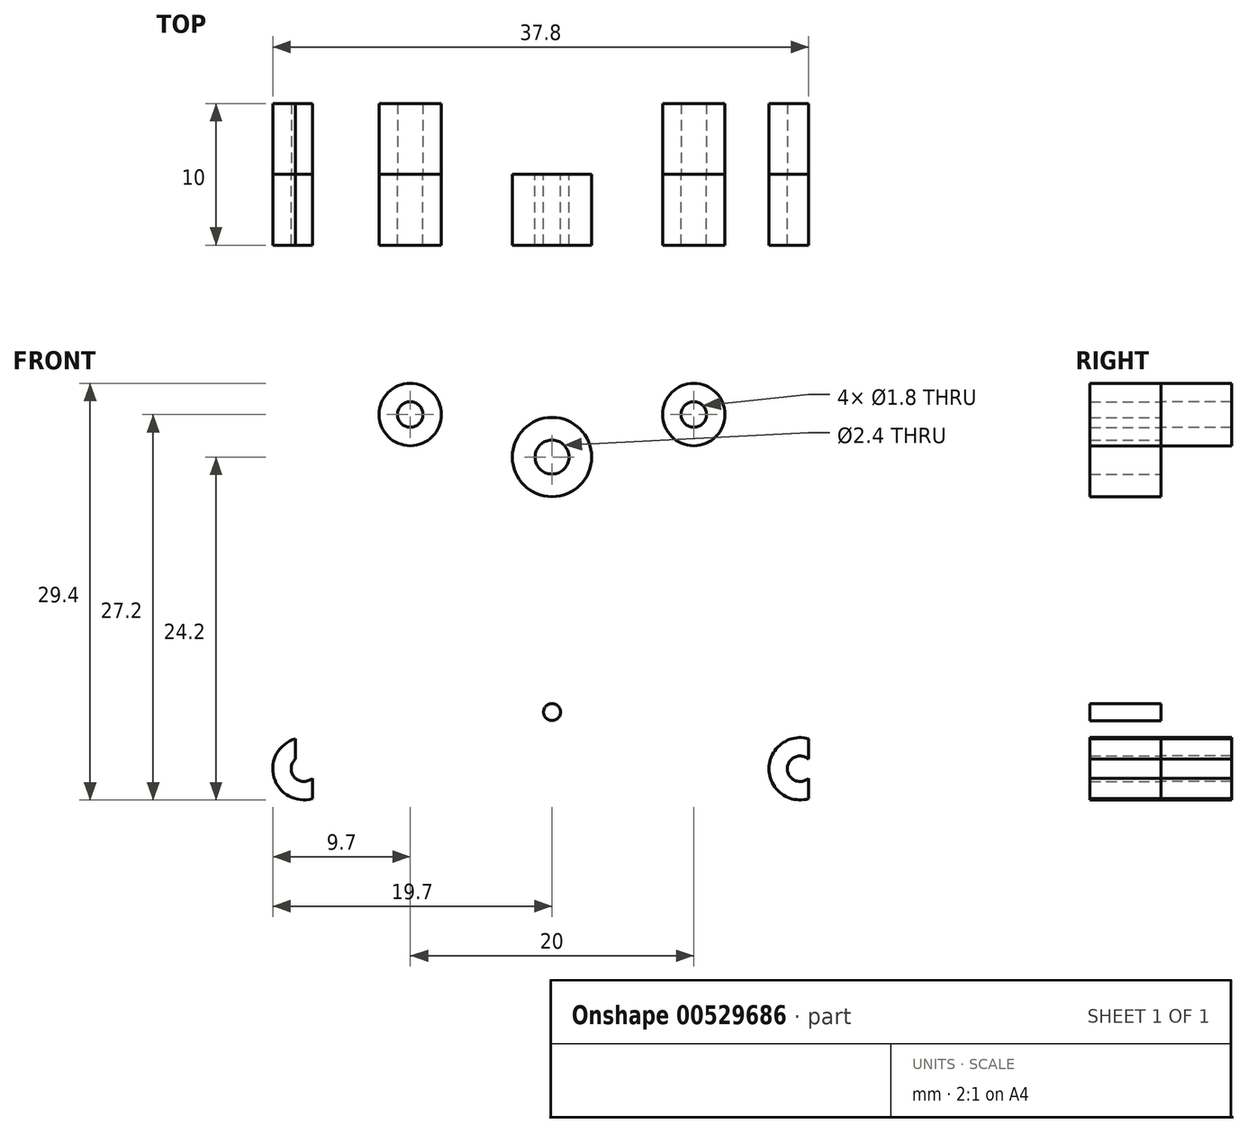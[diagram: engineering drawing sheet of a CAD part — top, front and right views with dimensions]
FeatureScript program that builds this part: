
annotation { "Feature Type Name" : "Feature", "Feature Type Description" : "" }
export const myFeature = defineFeature(function(context is Context, id is Id, definition is map)
    precondition{}
    {
        {
            var Q0;
            Q0=qCreatedBy(makeId("Front.planeOp"),FACE);
            var sketch = newSketch(context, id + "F0", { "sketchPlane" : qUnion([Q0])});
            skLineSegment(sketch, "E0", {"start": v(7.5, 25) * mm, "end": v(27.5, 25) * mm, "construction": true});
            skLineSegment(sketch, "E1", {"start": v(0, 0) * mm, "end": v(35, 0) * mm, "construction": true});
            skLineSegment(sketch, "E2", {"start": v(35, 0) * mm, "end": v(27.5, 25) * mm, "construction": true});
            skLineSegment(sketch, "E3", {"start": v(7.5, 25) * mm, "end": v(0, 0) * mm, "construction": true});
            skLineSegment(sketch, "E4", {"start": v(17.5, 25) * mm, "end": v(17.5, 0) * mm, "construction": true});
            skPoint(sketch, "E4.endSnap0", {"position": v(17.5, 0) * mm});
            skCircle(sketch, "E5", {"center": v(7.5, 25) * mm, "radius": 0.9 * mm});
            skCircle(sketch, "E6", {"center": v(27.5, 25) * mm, "radius": 0.9 * mm});
            skCircle(sketch, "E7", {"center": v(35, 0) * mm, "radius": 0.9 * mm});
            skCircle(sketch, "E8", {"center": v(0, 0) * mm, "radius": 0.9 * mm});
            skCircle(sketch, "E9", {"center": v(17.5, 22) * mm, "radius": 1.2 * mm});
            skCircle(sketch, "E10", {"center": v(17.5, 22) * mm, "radius": 2.8 * mm});
            skLineSegment(sketch, "E11.bottom", {"start": v(8.1, 22) * mm, "end": v(6.9, 22) * mm});
            skLineSegment(sketch, "E11.top", {"start": v(8.1, 28) * mm, "end": v(6.9, 28) * mm});
            skLineSegment(sketch, "E11.left", {"start": v(8.1, 22) * mm, "end": v(8.1, 28) * mm});
            skLineSegment(sketch, "E11.right", {"start": v(6.9, 22) * mm, "end": v(6.9, 28) * mm});
            skLineSegment(sketch, "E12.bottom", {"start": v(28.1, 22) * mm, "end": v(26.9, 22) * mm});
            skLineSegment(sketch, "E12.top", {"start": v(28.1, 28) * mm, "end": v(26.9, 28) * mm});
            skLineSegment(sketch, "E12.left", {"start": v(28.1, 22) * mm, "end": v(28.1, 28) * mm});
            skLineSegment(sketch, "E12.right", {"start": v(26.9, 22) * mm, "end": v(26.9, 28) * mm});
            skLineSegment(sketch, "E13.bottom", {"start": v(35.6, 3) * mm, "end": v(34.4, 3) * mm});
            skLineSegment(sketch, "E13.top", {"start": v(35.6, -3) * mm, "end": v(34.4, -3) * mm});
            skLineSegment(sketch, "E13.left", {"start": v(35.6, 3) * mm, "end": v(35.6, -3) * mm});
            skLineSegment(sketch, "E13.right", {"start": v(34.4, 3) * mm, "end": v(34.4, -3) * mm});
            skLineSegment(sketch, "E14.bottom", {"start": v(-0.6, 3) * mm, "end": v(0.6, 3) * mm});
            skLineSegment(sketch, "E14.top", {"start": v(-0.6, -3) * mm, "end": v(0.6, -3) * mm});
            skLineSegment(sketch, "E14.left", {"start": v(-0.6, 3) * mm, "end": v(-0.6, -3) * mm});
            skLineSegment(sketch, "E14.right", {"start": v(0.6, 3) * mm, "end": v(0.6, -3) * mm});
            skPoint(sketch, "E14.cornerSnap0", {"position": v(35, 3) * mm});
            skCircle(sketch, "E15", {"center": v(7.5, 25) * mm, "radius": 2.2 * mm});
            skCircle(sketch, "E16", {"center": v(27.5, 25) * mm, "radius": 2.2 * mm});
            skCircle(sketch, "E17", {"center": v(35, 0) * mm, "radius": 2.2 * mm});
            skCircle(sketch, "E18", {"center": v(0, 0) * mm, "radius": 2.2 * mm});
            skCircle(sketch, "E19", {"center": v(17.5, 4) * mm, "radius": 0.6 * mm});
            skSolve(sketch);
        }
        {
            var Q0;
            {var subQ0=sQuery(id+"F0.wireOp",EDGE,"E12.right");var subQ1=sQuery(id+"F0.wireOp",EDGE,"E6");var subQ2=makeQuery(id+"F0.imprint","INTERSECT",VERTEX,{"disambiguationData":[OD(0.0)],"derivedFrom":[subQ1,subQ0]});Q0=makeQuery(id+"F0.imprint","IMPRINT",FACE,{"disambiguationData":[TD([[makeQuery(id+"F0.imprint","IMPRINT",EDGE,{"disambiguationData":[TD([[subQ2,-1.0]])],"derivedFrom":subQ1}),-1.0]])]});}
            var Q1;
            {var subQ0=sQuery(id+"F0.wireOp",EDGE,"E12.right");var subQ1=sQuery(id+"F0.wireOp",EDGE,"E6");var subQ2=makeQuery(id+"F0.imprint","INTERSECT",VERTEX,{"disambiguationData":[OD(0.0)],"derivedFrom":[subQ1,subQ0]});Q1=makeQuery(id+"F0.imprint","IMPRINT",FACE,{"disambiguationData":[TD([[makeQuery(id+"F0.imprint","IMPRINT",EDGE,{"disambiguationData":[TD([[subQ2,1.0]])],"derivedFrom":subQ1}),-1.0]])]});}
            var Q2;
            {var subQ0=sQuery(id+"F0.wireOp",EDGE,"E12.left");var subQ1=sQuery(id+"F0.wireOp",EDGE,"E6");var subQ2=makeQuery(id+"F0.imprint","INTERSECT",VERTEX,{"disambiguationData":[OD(0.0)],"derivedFrom":[subQ1,subQ0]});Q2=makeQuery(id+"F0.imprint","IMPRINT",FACE,{"disambiguationData":[TD([[makeQuery(id+"F0.imprint","IMPRINT",EDGE,{"disambiguationData":[TD([[subQ2,1.0]])],"derivedFrom":subQ1}),-1.0]])]});}
            var Q3;
            {var subQ0=sQuery(id+"F0.wireOp",EDGE,"E12.right");var subQ1=sQuery(id+"F0.wireOp",EDGE,"E6");var subQ2=makeQuery(id+"F0.imprint","INTERSECT",VERTEX,{"disambiguationData":[OD(1.0)],"derivedFrom":[subQ1,subQ0]});Q3=makeQuery(id+"F0.imprint","IMPRINT",FACE,{"disambiguationData":[TD([[makeQuery(id+"F0.imprint","IMPRINT",EDGE,{"disambiguationData":[TD([[subQ2,-1.0]])],"derivedFrom":subQ1}),-1.0]])]});}
            var Q4;
            {var subQ0=sQuery(id+"F0.wireOp",EDGE,"E11.left");var subQ1=sQuery(id+"F0.wireOp",EDGE,"E5");var subQ2=makeQuery(id+"F0.imprint","INTERSECT",VERTEX,{"disambiguationData":[OD(0.0)],"derivedFrom":[subQ1,subQ0]});Q4=makeQuery(id+"F0.imprint","IMPRINT",FACE,{"disambiguationData":[TD([[makeQuery(id+"F0.imprint","IMPRINT",EDGE,{"disambiguationData":[TD([[subQ2,1.0]])],"derivedFrom":subQ1}),-1.0]])]});}
            var Q5;
            {var subQ0=sQuery(id+"F0.wireOp",EDGE,"E11.right");var subQ1=sQuery(id+"F0.wireOp",EDGE,"E5");var subQ2=makeQuery(id+"F0.imprint","INTERSECT",VERTEX,{"disambiguationData":[OD(0.0)],"derivedFrom":[subQ1,subQ0]});Q5=makeQuery(id+"F0.imprint","IMPRINT",FACE,{"disambiguationData":[TD([[makeQuery(id+"F0.imprint","IMPRINT",EDGE,{"disambiguationData":[TD([[subQ2,1.0]])],"derivedFrom":subQ1}),-1.0]])]});}
            var Q6;
            {var subQ0=sQuery(id+"F0.wireOp",EDGE,"E11.right");var subQ1=sQuery(id+"F0.wireOp",EDGE,"E5");var subQ2=makeQuery(id+"F0.imprint","INTERSECT",VERTEX,{"disambiguationData":[OD(0.0)],"derivedFrom":[subQ1,subQ0]});Q6=makeQuery(id+"F0.imprint","IMPRINT",FACE,{"disambiguationData":[TD([[makeQuery(id+"F0.imprint","IMPRINT",EDGE,{"disambiguationData":[TD([[subQ2,-1.0]])],"derivedFrom":subQ1}),-1.0]])]});}
            var Q7;
            {var subQ0=sQuery(id+"F0.wireOp",EDGE,"E11.right");var subQ1=sQuery(id+"F0.wireOp",EDGE,"E5");var subQ2=makeQuery(id+"F0.imprint","INTERSECT",VERTEX,{"disambiguationData":[OD(1.0)],"derivedFrom":[subQ1,subQ0]});Q7=makeQuery(id+"F0.imprint","IMPRINT",FACE,{"disambiguationData":[TD([[makeQuery(id+"F0.imprint","IMPRINT",EDGE,{"disambiguationData":[TD([[subQ2,-1.0]])],"derivedFrom":subQ1}),-1.0]])]});}
            var Q8;
            {var subQ0=sQuery(id+"F0.wireOp",EDGE,"E13.right");var subQ1=sQuery(id+"F0.wireOp",EDGE,"E7");var subQ2=makeQuery(id+"F0.imprint","INTERSECT",VERTEX,{"disambiguationData":[OD(0.0)],"derivedFrom":[subQ1,subQ0]});Q8=makeQuery(id+"F0.imprint","IMPRINT",FACE,{"disambiguationData":[TD([[makeQuery(id+"F0.imprint","IMPRINT",EDGE,{"disambiguationData":[TD([[subQ2,-1.0]])],"derivedFrom":subQ1}),-1.0]])]});}
            var Q9;
            {var subQ0=sQuery(id+"F0.wireOp",EDGE,"E13.right");var subQ1=sQuery(id+"F0.wireOp",EDGE,"E7");var subQ2=makeQuery(id+"F0.imprint","INTERSECT",VERTEX,{"disambiguationData":[OD(1.0)],"derivedFrom":[subQ1,subQ0]});Q9=makeQuery(id+"F0.imprint","IMPRINT",FACE,{"disambiguationData":[TD([[makeQuery(id+"F0.imprint","IMPRINT",EDGE,{"disambiguationData":[TD([[subQ2,-1.0]])],"derivedFrom":subQ1}),-1.0]])]});}
            var Q10;
            {var subQ0=sQuery(id+"F0.wireOp",EDGE,"E13.left");var subQ1=sQuery(id+"F0.wireOp",EDGE,"E7");var subQ2=makeQuery(id+"F0.imprint","INTERSECT",VERTEX,{"disambiguationData":[OD(0.0)],"derivedFrom":[subQ1,subQ0]});Q10=makeQuery(id+"F0.imprint","IMPRINT",FACE,{"disambiguationData":[TD([[makeQuery(id+"F0.imprint","IMPRINT",EDGE,{"disambiguationData":[TD([[subQ2,1.0]])],"derivedFrom":subQ1}),-1.0]])]});}
            var Q11;
            {var subQ0=sQuery(id+"F0.wireOp",EDGE,"E13.right");var subQ1=sQuery(id+"F0.wireOp",EDGE,"E7");var subQ2=makeQuery(id+"F0.imprint","INTERSECT",VERTEX,{"disambiguationData":[OD(0.0)],"derivedFrom":[subQ1,subQ0]});Q11=makeQuery(id+"F0.imprint","IMPRINT",FACE,{"disambiguationData":[TD([[makeQuery(id+"F0.imprint","IMPRINT",EDGE,{"disambiguationData":[TD([[subQ2,1.0]])],"derivedFrom":subQ1}),-1.0]])]});}
            var Q12;
            {var subQ0=sQuery(id+"F0.wireOp",EDGE,"E14.right");var subQ1=sQuery(id+"F0.wireOp",EDGE,"E8");var subQ2=makeQuery(id+"F0.imprint","INTERSECT",VERTEX,{"disambiguationData":[OD(0.0)],"derivedFrom":[subQ1,subQ0]});Q12=makeQuery(id+"F0.imprint","IMPRINT",FACE,{"disambiguationData":[TD([[makeQuery(id+"F0.imprint","IMPRINT",EDGE,{"disambiguationData":[TD([[subQ2,1.0]])],"derivedFrom":subQ1}),-1.0]])]});}
            var Q13;
            {var subQ0=sQuery(id+"F0.wireOp",EDGE,"E14.left");var subQ1=sQuery(id+"F0.wireOp",EDGE,"E8");var subQ2=makeQuery(id+"F0.imprint","INTERSECT",VERTEX,{"disambiguationData":[OD(0.0)],"derivedFrom":[subQ1,subQ0]});Q13=makeQuery(id+"F0.imprint","IMPRINT",FACE,{"disambiguationData":[TD([[makeQuery(id+"F0.imprint","IMPRINT",EDGE,{"disambiguationData":[TD([[subQ2,1.0]])],"derivedFrom":subQ1}),-1.0]])]});}
            var Q14;
            {var subQ0=sQuery(id+"F0.wireOp",EDGE,"E14.left");var subQ1=sQuery(id+"F0.wireOp",EDGE,"E8");var subQ2=makeQuery(id+"F0.imprint","INTERSECT",VERTEX,{"disambiguationData":[OD(0.0)],"derivedFrom":[subQ1,subQ0]});Q14=makeQuery(id+"F0.imprint","IMPRINT",FACE,{"disambiguationData":[TD([[makeQuery(id+"F0.imprint","IMPRINT",EDGE,{"disambiguationData":[TD([[subQ2,-1.0]])],"derivedFrom":subQ1}),-1.0]])]});}
            var Q15;
            {var subQ0=sQuery(id+"F0.wireOp",EDGE,"E14.left");var subQ1=sQuery(id+"F0.wireOp",EDGE,"E8");var subQ2=makeQuery(id+"F0.imprint","INTERSECT",VERTEX,{"disambiguationData":[OD(1.0)],"derivedFrom":[subQ1,subQ0]});Q15=makeQuery(id+"F0.imprint","IMPRINT",FACE,{"disambiguationData":[TD([[makeQuery(id+"F0.imprint","IMPRINT",EDGE,{"disambiguationData":[TD([[subQ2,-1.0]])],"derivedFrom":subQ1}),-1.0]])]});}
            extrude(context, id + "F1", {"entities" : qUnion([Q0, Q1, Q2, Q3, Q4, Q5, Q6, Q7, Q8, Q9, Q10, Q11, Q12, Q13, Q14, Q15]), "oppositeDirection" : true, "depth" : 5 * mm, "offsetDistance" : 25 * mm});
        }
        {
            var Q0;
            {var subQ0=sQuery(id+"F0.wireOp",EDGE,"E14.left");var subQ1=sQuery(id+"F0.wireOp",EDGE,"E8");var subQ2=makeQuery(id+"F0.imprint","INTERSECT",VERTEX,{"disambiguationData":[OD(0.0)],"derivedFrom":[subQ1,subQ0]});Q0=makeQuery(id+"F0.imprint","IMPRINT",FACE,{"disambiguationData":[TD([[makeQuery(id+"F0.imprint","IMPRINT",EDGE,{"disambiguationData":[TD([[subQ2,-1.0]])],"derivedFrom":subQ1}),-1.0]])]});}
            var Q1;
            {var subQ0=sQuery(id+"F0.wireOp",EDGE,"E14.right");var subQ1=sQuery(id+"F0.wireOp",EDGE,"E8");var subQ2=makeQuery(id+"F0.imprint","INTERSECT",VERTEX,{"disambiguationData":[OD(0.0)],"derivedFrom":[subQ1,subQ0]});Q1=makeQuery(id+"F0.imprint","IMPRINT",FACE,{"disambiguationData":[TD([[makeQuery(id+"F0.imprint","IMPRINT",EDGE,{"disambiguationData":[TD([[subQ2,1.0]])],"derivedFrom":subQ1}),-1.0]])]});}
            var Q2;
            {var subQ0=sQuery(id+"F0.wireOp",EDGE,"E14.left");var subQ1=sQuery(id+"F0.wireOp",EDGE,"E8");var subQ2=makeQuery(id+"F0.imprint","INTERSECT",VERTEX,{"disambiguationData":[OD(0.0)],"derivedFrom":[subQ1,subQ0]});Q2=makeQuery(id+"F0.imprint","IMPRINT",FACE,{"disambiguationData":[TD([[makeQuery(id+"F0.imprint","IMPRINT",EDGE,{"disambiguationData":[TD([[subQ2,1.0]])],"derivedFrom":subQ1}),-1.0]])]});}
            var Q3;
            {var subQ0=sQuery(id+"F0.wireOp",EDGE,"E14.left");var subQ1=sQuery(id+"F0.wireOp",EDGE,"E8");var subQ2=makeQuery(id+"F0.imprint","INTERSECT",VERTEX,{"disambiguationData":[OD(1.0)],"derivedFrom":[subQ1,subQ0]});Q3=makeQuery(id+"F0.imprint","IMPRINT",FACE,{"disambiguationData":[TD([[makeQuery(id+"F0.imprint","IMPRINT",EDGE,{"disambiguationData":[TD([[subQ2,-1.0]])],"derivedFrom":subQ1}),-1.0]])]});}
            var Q4;
            {var subQ0=sQuery(id+"F0.wireOp",EDGE,"E13.left");var subQ1=sQuery(id+"F0.wireOp",EDGE,"E7");var subQ2=makeQuery(id+"F0.imprint","INTERSECT",VERTEX,{"disambiguationData":[OD(0.0)],"derivedFrom":[subQ1,subQ0]});Q4=makeQuery(id+"F0.imprint","IMPRINT",FACE,{"disambiguationData":[TD([[makeQuery(id+"F0.imprint","IMPRINT",EDGE,{"disambiguationData":[TD([[subQ2,1.0]])],"derivedFrom":subQ1}),-1.0]])]});}
            var Q5;
            {var subQ0=sQuery(id+"F0.wireOp",EDGE,"E13.right");var subQ1=sQuery(id+"F0.wireOp",EDGE,"E7");var subQ2=makeQuery(id+"F0.imprint","INTERSECT",VERTEX,{"disambiguationData":[OD(0.0)],"derivedFrom":[subQ1,subQ0]});Q5=makeQuery(id+"F0.imprint","IMPRINT",FACE,{"disambiguationData":[TD([[makeQuery(id+"F0.imprint","IMPRINT",EDGE,{"disambiguationData":[TD([[subQ2,1.0]])],"derivedFrom":subQ1}),-1.0]])]});}
            var Q6;
            {var subQ0=sQuery(id+"F0.wireOp",EDGE,"E13.right");var subQ1=sQuery(id+"F0.wireOp",EDGE,"E7");var subQ2=makeQuery(id+"F0.imprint","INTERSECT",VERTEX,{"disambiguationData":[OD(0.0)],"derivedFrom":[subQ1,subQ0]});Q6=makeQuery(id+"F0.imprint","IMPRINT",FACE,{"disambiguationData":[TD([[makeQuery(id+"F0.imprint","IMPRINT",EDGE,{"disambiguationData":[TD([[subQ2,-1.0]])],"derivedFrom":subQ1}),-1.0]])]});}
            var Q7;
            {var subQ0=sQuery(id+"F0.wireOp",EDGE,"E13.right");var subQ1=sQuery(id+"F0.wireOp",EDGE,"E7");var subQ2=makeQuery(id+"F0.imprint","INTERSECT",VERTEX,{"disambiguationData":[OD(1.0)],"derivedFrom":[subQ1,subQ0]});Q7=makeQuery(id+"F0.imprint","IMPRINT",FACE,{"disambiguationData":[TD([[makeQuery(id+"F0.imprint","IMPRINT",EDGE,{"disambiguationData":[TD([[subQ2,-1.0]])],"derivedFrom":subQ1}),-1.0]])]});}
            var Q8;
            {var subQ0=sQuery(id+"F0.wireOp",EDGE,"E12.right");var subQ1=sQuery(id+"F0.wireOp",EDGE,"E6");var subQ2=makeQuery(id+"F0.imprint","INTERSECT",VERTEX,{"disambiguationData":[OD(0.0)],"derivedFrom":[subQ1,subQ0]});Q8=makeQuery(id+"F0.imprint","IMPRINT",FACE,{"disambiguationData":[TD([[makeQuery(id+"F0.imprint","IMPRINT",EDGE,{"disambiguationData":[TD([[subQ2,-1.0]])],"derivedFrom":subQ1}),-1.0]])]});}
            var Q9;
            {var subQ0=sQuery(id+"F0.wireOp",EDGE,"E12.right");var subQ1=sQuery(id+"F0.wireOp",EDGE,"E6");var subQ2=makeQuery(id+"F0.imprint","INTERSECT",VERTEX,{"disambiguationData":[OD(0.0)],"derivedFrom":[subQ1,subQ0]});Q9=makeQuery(id+"F0.imprint","IMPRINT",FACE,{"disambiguationData":[TD([[makeQuery(id+"F0.imprint","IMPRINT",EDGE,{"disambiguationData":[TD([[subQ2,1.0]])],"derivedFrom":subQ1}),-1.0]])]});}
            var Q10;
            {var subQ0=sQuery(id+"F0.wireOp",EDGE,"E12.left");var subQ1=sQuery(id+"F0.wireOp",EDGE,"E6");var subQ2=makeQuery(id+"F0.imprint","INTERSECT",VERTEX,{"disambiguationData":[OD(0.0)],"derivedFrom":[subQ1,subQ0]});Q10=makeQuery(id+"F0.imprint","IMPRINT",FACE,{"disambiguationData":[TD([[makeQuery(id+"F0.imprint","IMPRINT",EDGE,{"disambiguationData":[TD([[subQ2,1.0]])],"derivedFrom":subQ1}),-1.0]])]});}
            var Q11;
            {var subQ0=sQuery(id+"F0.wireOp",EDGE,"E12.right");var subQ1=sQuery(id+"F0.wireOp",EDGE,"E6");var subQ2=makeQuery(id+"F0.imprint","INTERSECT",VERTEX,{"disambiguationData":[OD(1.0)],"derivedFrom":[subQ1,subQ0]});Q11=makeQuery(id+"F0.imprint","IMPRINT",FACE,{"disambiguationData":[TD([[makeQuery(id+"F0.imprint","IMPRINT",EDGE,{"disambiguationData":[TD([[subQ2,-1.0]])],"derivedFrom":subQ1}),-1.0]])]});}
            var Q12;
            Q12=makeQuery(id+"F0.imprint","IMPRINT",FACE,{"disambiguationData":[TD([[makeQuery(id+"F0.imprint","IMPRINT",EDGE,{"derivedFrom":sQuery(id+"F0.wireOp",EDGE,"E9")}),-1.0]])]});
            var Q13;
            {var subQ0=sQuery(id+"F0.wireOp",EDGE,"E11.left");var subQ1=sQuery(id+"F0.wireOp",EDGE,"E5");var subQ2=makeQuery(id+"F0.imprint","INTERSECT",VERTEX,{"disambiguationData":[OD(0.0)],"derivedFrom":[subQ1,subQ0]});Q13=makeQuery(id+"F0.imprint","IMPRINT",FACE,{"disambiguationData":[TD([[makeQuery(id+"F0.imprint","IMPRINT",EDGE,{"disambiguationData":[TD([[subQ2,1.0]])],"derivedFrom":subQ1}),-1.0]])]});}
            var Q14;
            {var subQ0=sQuery(id+"F0.wireOp",EDGE,"E11.right");var subQ1=sQuery(id+"F0.wireOp",EDGE,"E5");var subQ2=makeQuery(id+"F0.imprint","INTERSECT",VERTEX,{"disambiguationData":[OD(0.0)],"derivedFrom":[subQ1,subQ0]});Q14=makeQuery(id+"F0.imprint","IMPRINT",FACE,{"disambiguationData":[TD([[makeQuery(id+"F0.imprint","IMPRINT",EDGE,{"disambiguationData":[TD([[subQ2,1.0]])],"derivedFrom":subQ1}),-1.0]])]});}
            var Q15;
            {var subQ0=sQuery(id+"F0.wireOp",EDGE,"E11.right");var subQ1=sQuery(id+"F0.wireOp",EDGE,"E5");var subQ2=makeQuery(id+"F0.imprint","INTERSECT",VERTEX,{"disambiguationData":[OD(1.0)],"derivedFrom":[subQ1,subQ0]});Q15=makeQuery(id+"F0.imprint","IMPRINT",FACE,{"disambiguationData":[TD([[makeQuery(id+"F0.imprint","IMPRINT",EDGE,{"disambiguationData":[TD([[subQ2,-1.0]])],"derivedFrom":subQ1}),-1.0]])]});}
            var Q16;
            {var subQ0=sQuery(id+"F0.wireOp",EDGE,"E11.right");var subQ1=sQuery(id+"F0.wireOp",EDGE,"E5");var subQ2=makeQuery(id+"F0.imprint","INTERSECT",VERTEX,{"disambiguationData":[OD(0.0)],"derivedFrom":[subQ1,subQ0]});Q16=makeQuery(id+"F0.imprint","IMPRINT",FACE,{"disambiguationData":[TD([[makeQuery(id+"F0.imprint","IMPRINT",EDGE,{"disambiguationData":[TD([[subQ2,-1.0]])],"derivedFrom":subQ1}),-1.0]])]});}
            var Q17;
            Q17=makeQuery(id+"F0.imprint","IMPRINT",FACE,{"disambiguationData":[TD([[makeQuery(id+"F0.imprint","IMPRINT",EDGE,{"derivedFrom":sQuery(id+"F0.wireOp",EDGE,"E19")}),1.0]])]});
            extrude(context, id + "F2", {"entities" : qUnion([Q0, Q1, Q2, Q3, Q4, Q5, Q6, Q7, Q8, Q9, Q10, Q11, Q12, Q13, Q14, Q15, Q16, Q17]), "depth" : 5 * mm, "offsetDistance" : 25 * mm});
        }
    });
